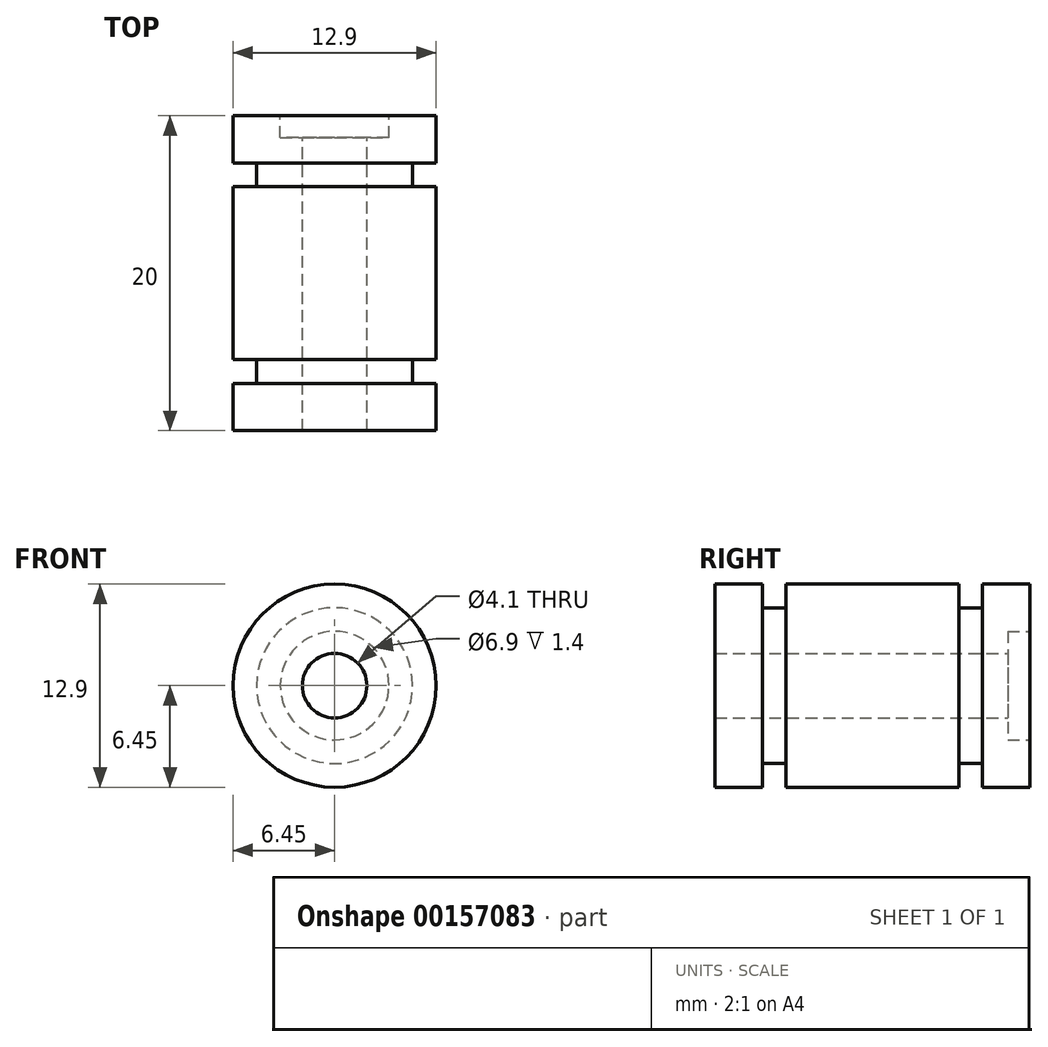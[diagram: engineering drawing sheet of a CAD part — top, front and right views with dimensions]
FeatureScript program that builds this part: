
annotation { "Feature Type Name" : "Feature", "Feature Type Description" : "" }
export const myFeature = defineFeature(function(context is Context, id is Id, definition is map)
    precondition{}
    {
        {
            var Q0;
            Q0=qCreatedBy(makeId("Right.planeOp"),FACE);
            var sketch = newSketch(context, id + "F0", { "sketchPlane" : qUnion([Q0])});
            skLineSegment(sketch, "E0", {"start": v(11.47, 0) * mm, "end": v(0, 0) * mm, "construction": true});
            skLineSegment(sketch, "E1", {"start": v(18.6, 2.05) * mm, "end": v(0, 2.05) * mm});
            skLineSegment(sketch, "E2", {"start": v(18.6, 2.05) * mm, "end": v(18.6, 3.45) * mm});
            skLineSegment(sketch, "E3", {"start": v(20, 3.45) * mm, "end": v(18.6, 3.45) * mm});
            skLineSegment(sketch, "E4", {"start": v(20, 3.45) * mm, "end": v(20, 6.45) * mm});
            skLineSegment(sketch, "E5", {"start": v(17, 6.45) * mm, "end": v(20, 6.45) * mm});
            skLineSegment(sketch, "E6", {"start": v(17, 6.45) * mm, "end": v(17, 4.95) * mm});
            skLineSegment(sketch, "E7", {"start": v(15.5, 4.95) * mm, "end": v(17, 4.95) * mm});
            skLineSegment(sketch, "E8", {"start": v(3, 4.95) * mm, "end": v(3, 6.45) * mm});
            skLineSegment(sketch, "E9", {"start": v(0, 6.45) * mm, "end": v(3, 6.45) * mm});
            skLineSegment(sketch, "E10", {"start": v(0, 6.45) * mm, "end": v(0, 2.05) * mm});
            skLineSegment(sketch, "E11", {"start": v(4.5, 4.95) * mm, "end": v(4.5, 6.45) * mm});
            skLineSegment(sketch, "E12", {"start": v(4.5, 6.45) * mm, "end": v(15.5, 6.45) * mm});
            skLineSegment(sketch, "E13", {"start": v(15.5, 6.45) * mm, "end": v(15.5, 4.95) * mm});
            skLineSegment(sketch, "E14.trimOffspring", {"start": v(4.5, 4.95) * mm, "end": v(3, 4.95) * mm});
            skSolve(sketch);
        }
        {
            var Q0;
            Q0=makeQuery(id+"F0.imprint","IMPRINT",FACE,{"disambiguationData":[TD([[makeQuery(id+"F0.imprint","IMPRINT",EDGE,{"derivedFrom":sQuery(id+"F0.wireOp",EDGE,"E1")}),-1.0]])]});
            var Q1;
            Q1=sQuery(id+"F0.wireOp",EDGE,"E0");
            revolve(context, id + "F1", {"entities" : qUnion([Q0]), "axis" : qUnion([Q1]), "revolveType" : RevolveType.FULL});
        }
    });
